# Revit family: Faucet-American_Standard-Aspirations-7061461_Series
name_source: partatom
category: Plumbing Fixtures
units: mm (PartAtom-declared; Revit-internal decimal feet)

## family parameters
Cut with Voids When Loaded = No
Host = Face
OmniClass Number = 23.45.55.14
OmniClass Title = Single Faucets
Part Type = Normal
Room Calculation Point = No
Round Connector Dimension = Use Diameter
Shared = Yes

## types (3) — shared parameters
ADA Compliant = Yes
ANSI A117.1 = Yes
ASME A112.18.1/CSA B125.1 = Yes
Assembly Code = D2020300
CWFU = 1.5
Compliance Certifications = These products meet or exceed the following codes and standards: ASSE 1016, ASME A112.18.1, CSA B125.1
Default Elevation = 0"
Description = Aspirations™ Single Control Wall Mount Faucet
Drain Max/Min Length = 1"
HW Connection = No
HWFU = 1.5
Height = 7 7/8"
Installation Type = Wall Mounted
Length = 8"
Manufacturer = American Standard
Max. Flow Rate = 1.2 gpm/4.5 L/min
NSF/ANSI/CAN 372 = Yes
NSF/ANSI/CAN 61 = Yes
Tempered Water Connection = Yes
URL = https://www.americanstandard-us.com
Vent Connection = No
WFU = 2
Waste Connection = No
Waste Connection Diameter = 1 1/4"
Water Connection Diameter = 1/2"
Width = 6 7/16"

## per-type parameters (varying)
| type | CW Connection | Drain Depth | Drain Height | Drain Width | Finish | Material |
| 7061461.002 | No | 7" | 1" | 6" | Brass-American Standard-002-Polished Chrome | Brass-American Standard-002-Polished Chrome |
| 7061461.295 | Yes | 8 1/32" | 0" | 4 3/4" | Brass-American Standard-243-Matte Black | Brass-American Standard-243-Matte Black |
| 7061461.243 | No | 8 1/32" | 0" | 4 3/4" | Brass-American Standard-295-Satin Nickel | Brass-American Standard-295-Satin Nickel |

note: column(s) folded — value = type name in every type: Model

## geometry (parser evidence)
native form markers: Sweep x2
no freeform markers — native parametric forms only
